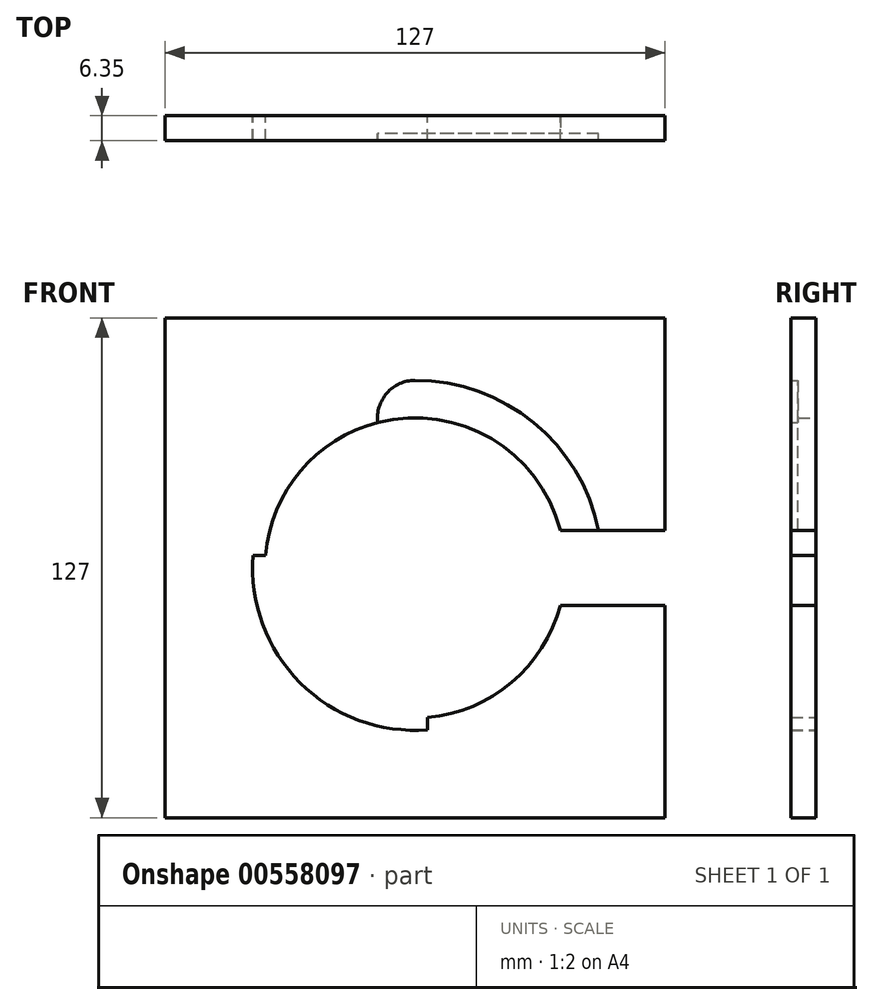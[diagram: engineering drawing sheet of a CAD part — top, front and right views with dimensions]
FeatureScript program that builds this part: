
annotation { "Feature Type Name" : "Feature", "Feature Type Description" : "" }
export const myFeature = defineFeature(function(context is Context, id is Id, definition is map)
    precondition{}
    {
        {
            var Q0;
            Q0=qCreatedBy(makeId("Front.planeOp"),FACE);
            var sketch = newSketch(context, id + "F0", { "sketchPlane" : qUnion([Q0])});
            skLineSegment(sketch, "E0.bottom", {"start": v(63.5, -63.5) * mm, "end": v(-63.5, -63.5) * mm});
            skLineSegment(sketch, "E0.top", {"start": v(63.5, 63.5) * mm, "end": v(-63.5, 63.5) * mm});
            skLineSegment(sketch, "E0.left", {"start": v(63.5, -63.5) * mm, "end": v(63.5, -9.53) * mm});
            skLineSegment(sketch, "E0.right", {"start": v(-63.5, -63.5) * mm, "end": v(-63.5, 63.5) * mm});
            skPoint(sketch, "E0.middle", {"position": v(0, 0) * mm});
            skArc(sketch, "E1", {"start": v(-9.45, 36.9) * mm, "mid": v(-29.1, 24.6) * mm, "end": v(-37.97, 3.17) * mm});
            skArc(sketch, "E2", {"start": v(46.66, 9.52) * mm, "mid": v(30.12, 36.9) * mm, "end": v(0, 47.63) * mm});
            skArc(sketch, "E3", {"start": v(0, 47.62) * mm, "mid": v(-7.14, 44.4) * mm, "end": v(-9.45, 36.9) * mm});
            skArc(sketch, "E4", {"start": v(-41.15, 3.17) * mm, "mid": v(-29.19, -29.19) * mm, "end": v(3.18, -41.15) * mm});
            skLineSegment(sketch, "E5.bottom", {"start": v(63.5, -9.53) * mm, "end": v(45.03, -9.53) * mm});
            skLineSegment(sketch, "E5.top", {"start": v(63.5, 9.52) * mm, "end": v(46.66, 9.52) * mm});
            skPoint(sketch, "E5.middle", {"position": v(63.5, 0) * mm});
            skLineSegment(sketch, "E6.trimOffspring", {"start": v(63.5, 9.53) * mm, "end": v(63.5, 63.5) * mm});
            skPoint(sketch, "E7.orphan", {"position": v(81.97, -9.52) * mm});
            skPoint(sketch, "E8.orphan", {"position": v(81.97, 9.53) * mm});
            skPoint(sketch, "E9.orphan", {"position": v(45.03, 9.52) * mm});
            skLineSegment(sketch, "E10.bottom", {"start": v(63.5, 9.52) * mm, "end": v(45.03, 9.52) * mm});
            skLineSegment(sketch, "E10.top", {"start": v(63.5, -9.52) * mm, "end": v(36.9, -9.52) * mm});
            skLineSegment(sketch, "E11.left", {"start": v(3.18, -41.15) * mm, "end": v(3.18, -37.97) * mm});
            skPoint(sketch, "E11.top.end.orphan", {"position": v(-3.18, 45.56) * mm});
            skPoint(sketch, "E12.orphan", {"position": v(3.18, 45.56) * mm});
            skArc(sketch, "E13.trimOffspring", {"start": v(3.18, -37.97) * mm, "mid": v(24.57, -29.12) * mm, "end": v(36.9, -9.52) * mm});
            skPoint(sketch, "E11.bottom.start.orphan", {"position": v(3.17, -45.56) * mm});
            skPoint(sketch, "E14.orphan", {"position": v(-3.17, -45.56) * mm});
            skLineSegment(sketch, "E15.top", {"start": v(-37.97, 3.17) * mm, "end": v(-41.15, 3.17) * mm});
            skPoint(sketch, "E16.orphan", {"position": v(43.74, 3.18) * mm});
            skPoint(sketch, "E17.orphan", {"position": v(43.74, -3.17) * mm});
            skPoint(sketch, "E15.right.end.orphan", {"position": v(-43.74, 3.17) * mm});
            skPoint(sketch, "E18.orphan", {"position": v(-43.74, -3.18) * mm});
            skPoint(sketch, "E19.center.orphan", {"position": v(38.1, 0) * mm});
            skSolve(sketch);
        }
        {
            var Q0;
            Q0 = qSketchRegion(id + "F0", true);
            extrude(context, id + "F1", {"entities" : qUnion([Q0]), "depth" : 1.78 * mm, "offsetDistance" : 25.4 * mm});
        }
        {
            var Q0;
            Q0=qCreatedBy(makeId("Front.planeOp"),FACE);
            var sketch = newSketch(context, id + "F2", { "sketchPlane" : qUnion([Q0])});
            skLineSegment(sketch, "E20.bottom", {"start": v(-63.5, -63.5) * mm, "end": v(63.5, -63.5) * mm});
            skLineSegment(sketch, "E20.top", {"start": v(-63.5, 63.5) * mm, "end": v(63.5, 63.5) * mm});
            skLineSegment(sketch, "E20.left", {"start": v(-63.5, -63.5) * mm, "end": v(-63.5, 63.5) * mm});
            skLineSegment(sketch, "E20.right", {"start": v(63.5, -63.5) * mm, "end": v(63.5, -9.52) * mm});
            skPoint(sketch, "E20.middle", {"position": v(0, 0) * mm});
            skArc(sketch, "E21", {"start": v(36.9, 9.53) * mm, "mid": v(-3.22, 37.96) * mm, "end": v(-37.97, 3.17) * mm});
            skLineSegment(sketch, "E22.bottom", {"start": v(63.5, -9.52) * mm, "end": v(36.9, -9.52) * mm});
            skLineSegment(sketch, "E22.top", {"start": v(63.5, 9.53) * mm, "end": v(36.9, 9.53) * mm});
            skLineSegment(sketch, "E23.trimOffspring", {"start": v(63.5, 9.53) * mm, "end": v(63.5, 63.5) * mm});
            skPoint(sketch, "E24.orphan", {"position": v(67.4, 9.53) * mm});
            skPoint(sketch, "E25.orphan", {"position": v(67.4, -9.52) * mm});
            skPoint(sketch, "E22.right.start.orphan", {"position": v(-67.4, -9.53) * mm});
            skPoint(sketch, "E26.orphan", {"position": v(-67.4, 9.52) * mm});
            skLineSegment(sketch, "E27.top", {"start": v(-41.15, 3.17) * mm, "end": v(-37.97, 3.17) * mm});
            skPoint(sketch, "E28.orphan", {"position": v(48.33, 3.17) * mm});
            skPoint(sketch, "E29.orphan", {"position": v(48.33, -3.18) * mm});
            skArc(sketch, "E30.trimOffspring", {"start": v(3.18, -37.97) * mm, "mid": v(24.57, -29.12) * mm, "end": v(36.9, -9.52) * mm});
            skArc(sketch, "E31.trimOffspring", {"start": v(-41.15, 3.17) * mm, "mid": v(-29.19, -29.19) * mm, "end": v(3.18, -41.15) * mm});
            skPoint(sketch, "E27.left.end.orphan", {"position": v(-48.33, 3.18) * mm});
            skPoint(sketch, "E32.orphan", {"position": v(-48.33, -3.17) * mm});
            skLineSegment(sketch, "E33.right", {"start": v(3.18, -41.15) * mm, "end": v(3.18, -37.97) * mm});
            skPoint(sketch, "E33.cornerSnap0", {"position": v(-3.18, -41.15) * mm});
            skPoint(sketch, "E34.orphan", {"position": v(-3.18, 44.63) * mm});
            skPoint(sketch, "E35.orphan", {"position": v(3.18, 44.63) * mm});
            skPoint(sketch, "E33.bottom.start.orphan", {"position": v(-3.18, -44.63) * mm});
            skPoint(sketch, "E36.orphan", {"position": v(3.18, -44.63) * mm});
            skSolve(sketch);
        }
        {
            var Q0;
            Q0 = qSketchRegion(id + "F2", true);
            extrude(context, id + "F3", {"entities" : qUnion([Q0]), "operationType" : NewBodyOperationType.ADD, "oppositeDirection" : true, "depth" : 4.57 * mm, "offsetDistance" : 25.4 * mm});
        }
    });
